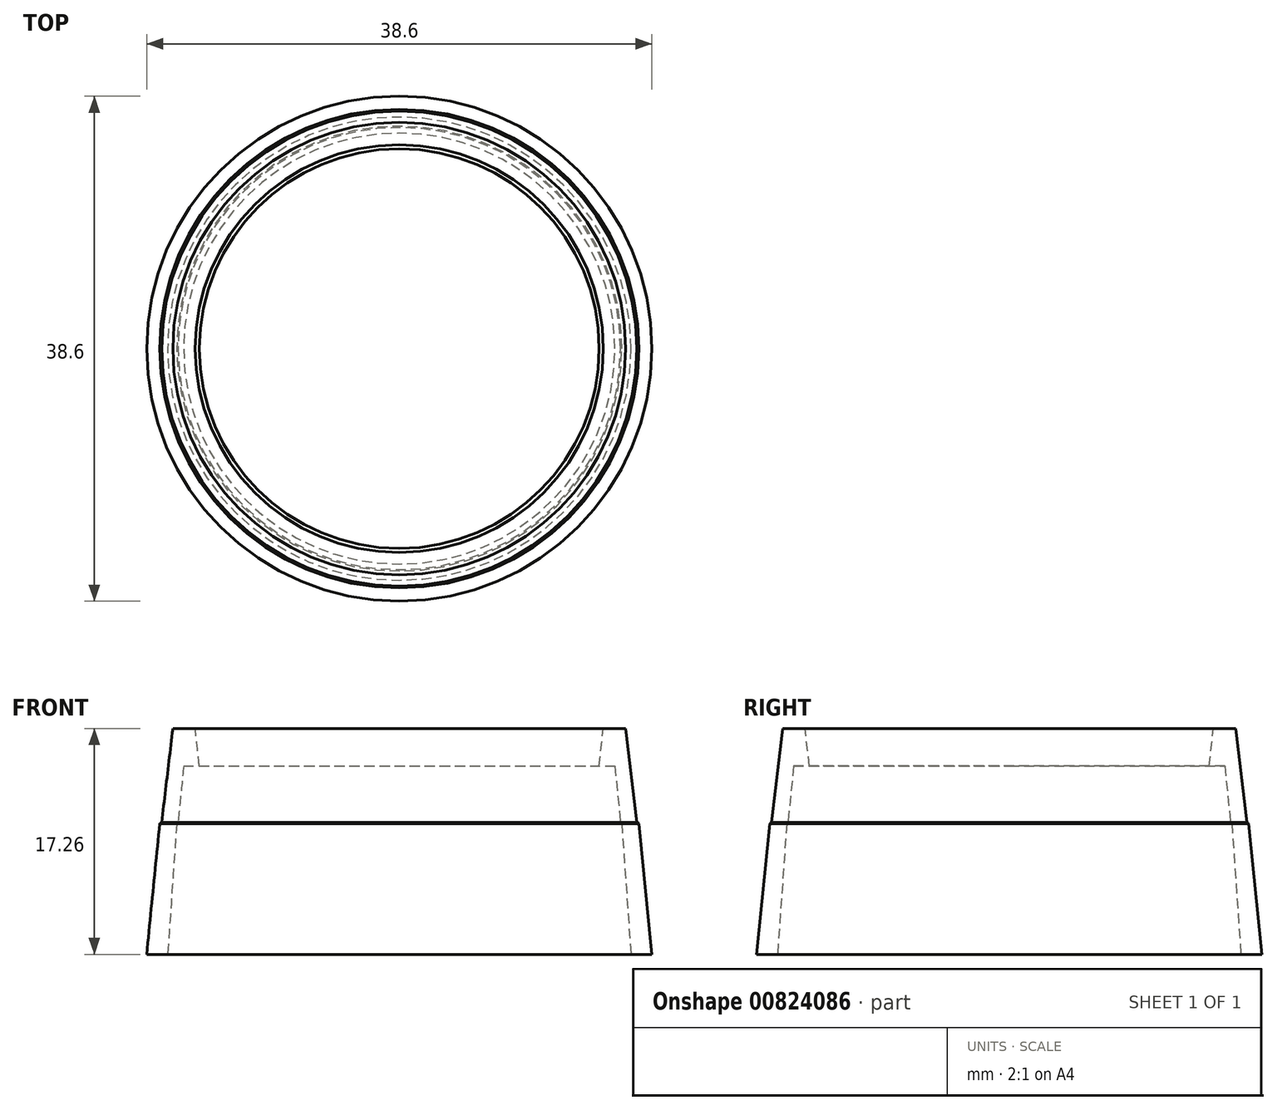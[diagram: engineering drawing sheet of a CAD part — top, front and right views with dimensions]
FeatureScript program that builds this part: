
annotation { "Feature Type Name" : "Feature", "Feature Type Description" : "" }
export const myFeature = defineFeature(function(context is Context, id is Id, definition is map)
    precondition{}
    {
        {
            var Q0;
            Q0=qCreatedBy(makeId("Front.planeOp"),FACE);
            var sketch = newSketch(context, id + "F0", { "sketchPlane" : qUnion([Q0])});
            skLineSegment(sketch, "E0", {"start": v(0, 0) * mm, "end": v(0, 17.26) * mm});
            skLineSegment(sketch, "E1", {"start": v(0, 17.26) * mm, "end": v(-17.3, 17.26) * mm, "construction": true});
            skLineSegment(sketch, "E2", {"start": v(0, 0) * mm, "end": v(-19.3, 0) * mm, "construction": true});
            skLineSegment(sketch, "E3", {"start": v(0, 17.26) * mm, "end": v(0, 10.1) * mm});
            skLineSegment(sketch, "E4", {"start": v(0, 10.1) * mm, "end": v(-18.15, 10.1) * mm, "construction": true});
            skLineSegment(sketch, "E5", {"start": v(0, 0) * mm, "end": v(0, 10) * mm});
            skLineSegment(sketch, "E6", {"start": v(0, 10) * mm, "end": v(-18.3, 10) * mm, "construction": true});
            skLineSegment(sketch, "E7", {"start": v(-18.3, 10) * mm, "end": v(-19.3, 0) * mm});
            skLineSegment(sketch, "E8", {"start": v(-18.3, 10) * mm, "end": v(-18.15, 10.1) * mm});
            skLineSegment(sketch, "E9", {"start": v(-18.15, 10.1) * mm, "end": v(-17.3, 17.26) * mm});
            skLineSegment(sketch, "E10", {"start": v(-19.3, 0) * mm, "end": v(-17.7, 0) * mm});
            skLineSegment(sketch, "E11", {"start": v(-17.7, 0) * mm, "end": v(-17, 10) * mm});
            skLineSegment(sketch, "E12", {"start": v(-17, 10) * mm, "end": v(-16.9, 10.1) * mm});
            skLineSegment(sketch, "E13", {"start": v(-16.9, 10.1) * mm, "end": v(-16.47, 14.39) * mm});
            skLineSegment(sketch, "E14", {"start": v(-16.47, 14.39) * mm, "end": v(-15.27, 14.39) * mm});
            skLineSegment(sketch, "E15", {"start": v(-15.27, 14.39) * mm, "end": v(-15.6, 17.26) * mm});
            skLineSegment(sketch, "E16", {"start": v(-15.6, 17.26) * mm, "end": v(-17.3, 17.26) * mm});
            skSolve(sketch);
        }
        {
            var Q0;
            Q0=qCreatedBy(makeId("Front.planeOp"),FACE);
            var sketch = newSketch(context, id + "F1", { "sketchPlane" : qUnion([Q0])});
            skLineSegment(sketch, "E17.0", {"start": v(-18.15, 10.1) * mm, "end": v(-17.3, 17.26) * mm});
            skLineSegment(sketch, "E18.0", {"start": v(-18.3, 10) * mm, "end": v(-18.15, 10.1) * mm});
            skLineSegment(sketch, "E19.0", {"start": v(-18.3, 10) * mm, "end": v(-19.3, 0) * mm});
            skLineSegment(sketch, "E20.0", {"start": v(-19.3, 0) * mm, "end": v(-17.7, 0) * mm});
            skLineSegment(sketch, "E21.0", {"start": v(-17.7, 0) * mm, "end": v(-17, 10) * mm});
            skLineSegment(sketch, "E22.0", {"start": v(-17, 10) * mm, "end": v(-16.9, 10.1) * mm});
            skLineSegment(sketch, "E23.0", {"start": v(-16.9, 10.1) * mm, "end": v(-16.47, 14.4) * mm});
            skLineSegment(sketch, "E24.0", {"start": v(-16.47, 14.39) * mm, "end": v(-15.27, 14.39) * mm});
            skLineSegment(sketch, "E25.0", {"start": v(-15.27, 14.39) * mm, "end": v(-15.6, 17.26) * mm});
            skLineSegment(sketch, "E26.0", {"start": v(-15.6, 17.26) * mm, "end": v(-17.3, 17.26) * mm});
            skSolve(sketch);
        }
        {
            var Q0;
            Q0 = qSketchRegion(id + "F1", true);
            var Q1;
            Q1=sQuery(id+"F0.wireOp",EDGE,"E5");
            revolve(context, id + "F2", {"surfaceOperationType" : NewSurfaceOperationType.NEW, "entities" : qUnion([Q0]), "axis" : qUnion([Q1]), "revolveType" : RevolveType.FULL});
        }
        {
            var Q0;
            Q0=makeQuery(id+"F2.opRevolve","SWEPT_FACE",FACE,{"disambiguationData":[OSD([sQuery(id+"F1.wireOp",EDGE,"E20.0")])]});
            var sketch = newSketch(context, id + "F3", { "sketchPlane" : qUnion([Q0])});
            skLineSegment(sketch, "E27", {"start": v(0, 0) * mm, "end": v(-19.3, 0) * mm});
            skLineSegment(sketch, "E28", {"start": v(-19.3, 0) * mm, "end": v(0, 0) * mm});
            skLineSegment(sketch, "E29", {"start": v(0, 19.3) * mm, "end": v(0, 0) * mm});
            skLineSegment(sketch, "E30", {"start": v(0, 0) * mm, "end": v(19.3, 0) * mm});
            skLineSegment(sketch, "E31", {"start": v(0, 0) * mm, "end": v(0, -19.3) * mm});
            skLineSegment(sketch, "E32", {"start": v(0, 0) * mm, "end": v(-7.27, -17.88) * mm});
            skLineSegment(sketch, "E33", {"start": v(-7.27, -17.88) * mm, "end": v(0, 0) * mm});
            skLineSegment(sketch, "E34", {"start": v(0, 0) * mm, "end": v(-17.88, -7.27) * mm});
            skLineSegment(sketch, "E35", {"start": v(0, 0) * mm, "end": v(-13.65, -13.65) * mm});
            skArc(sketch, "E36", {"start": v(-17.88, -7.27) * mm, "mid": v(-13.65, -13.65) * mm, "end": v(-7.27, -17.88) * mm, "construction": true});
            skCircle(sketch, "E37", {"center": v(-7.82, -17.64) * mm, "radius": 0.6 * mm});
            skCircle(sketch, "E38", {"center": v(-17.64, -7.82) * mm, "radius": 0.6 * mm});
            skCircle(sketch, "E39", {"center": v(-13.65, -13.65) * mm, "radius": 0.6 * mm});
            skArc(sketch, "E40", {"start": v(-13.65, -13.65) * mm, "mid": v(-10.67, -16.08) * mm, "end": v(-7.27, -17.88) * mm});
            skArc(sketch, "E41", {"start": v(-17.88, -7.27) * mm, "mid": v(-16.08, -10.67) * mm, "end": v(-13.65, -13.65) * mm});
            skCircle(sketch, "E42", {"center": v(-10.67, -16.08) * mm, "radius": 0.6 * mm});
            skCircle(sketch, "E43", {"center": v(-16.08, -10.67) * mm, "radius": 0.6 * mm});
            skSolve(sketch);
        }
        {
            var Q0;
            Q0=sQuery(id+"F3.wireOp",EDGE,"E34");
            var Q1;
            Q1=sQuery(id+"F0.wireOp",EDGE,"E3");
            cPlane(context, id + "F4", {"entities" : qUnion([Q0, Q1]), "cplaneType" : CPlaneType.LINE_ANGLE, "offset" : 25 * mm, "angle" : 0 * degree, "width" : 150 * mm, "height" : 150 * mm});
        }
        {
            var Q0;
            Q0=qCreatedBy(id+"F4.planeOp",FACE);
            cPlane(context, id + "F5", {"entities" : qUnion([Q0]), "cplaneType" : CPlaneType.OFFSET, "offset" : 0 * mm, "width" : 150 * mm, "height" : 150 * mm});
        }
        {
            var Q0;
            Q0=qCreatedBy(makeId("Top.planeOp"),FACE);
            cPlane(context, id + "F6", {"entities" : qUnion([Q0]), "cplaneType" : CPlaneType.OFFSET, "offset" : 10 * mm, "width" : 150 * mm, "height" : 150 * mm});
        }
    });
